# Revit family: Window-Fixed-Duratherm-Fixed_Frame-Wood
name_source: partatom
category: Windows
revit_build: Autodesk Revit Architecture 2012 (Build: 20110916_2132(x64)
units: mm (PartAtom-declared; Revit-internal decimal feet)

## types (1)
- Window-Fixed-Duratherm-Fixed_Frame-Wood
    Air Leakage = 0.007
    Assembly Code = B2020130
    Custom Frame Depth = 6 1/4"
    Custom Frame Depth Desired = No
    Default Sill Height = 3' - 0"
    Description = Wood window with 1" insulated glazing. Contact manufacturer for customized needs.
    Design Pressure = DP40
    Desired Height = 4' - 0"
    Desired Width = 3' - 0"
    Energy Star Zone = N,NC,SC,S
    Frame Depth = 6 1/4"
    Glazing = Low E
    Glazing Opening Size SF = 10.04 SF
    Height = 4' - 0"
    LEED Credit = MR Credit 7
    Manufacturer = Duratherm Window Corporation
    Model = Fixed Frame
    Nosing Required = No
    Operation = Fixed
    Product Documentation Link = http://www.durathermwindow.com
    R Value = 3.03
    Rough Height = 4' - 1"
    Rough Width = 3' - 1"
    Sill Thickness = 1"
    Solar Heat Gain Coefficient = 0.38
    Style = Fixed
    Type Comments = 36" x 48" Fixed Frame Wood Window with Nosing
    U Value = 0.33
    URL = www.durathermwindow.com
    Visible Light Transmission = 0.7
    Wall Closure = By host
    Width = 3' - 0"

## geometry (parser evidence)
native form markers: Sweep x1
no freeform markers — native parametric forms only
